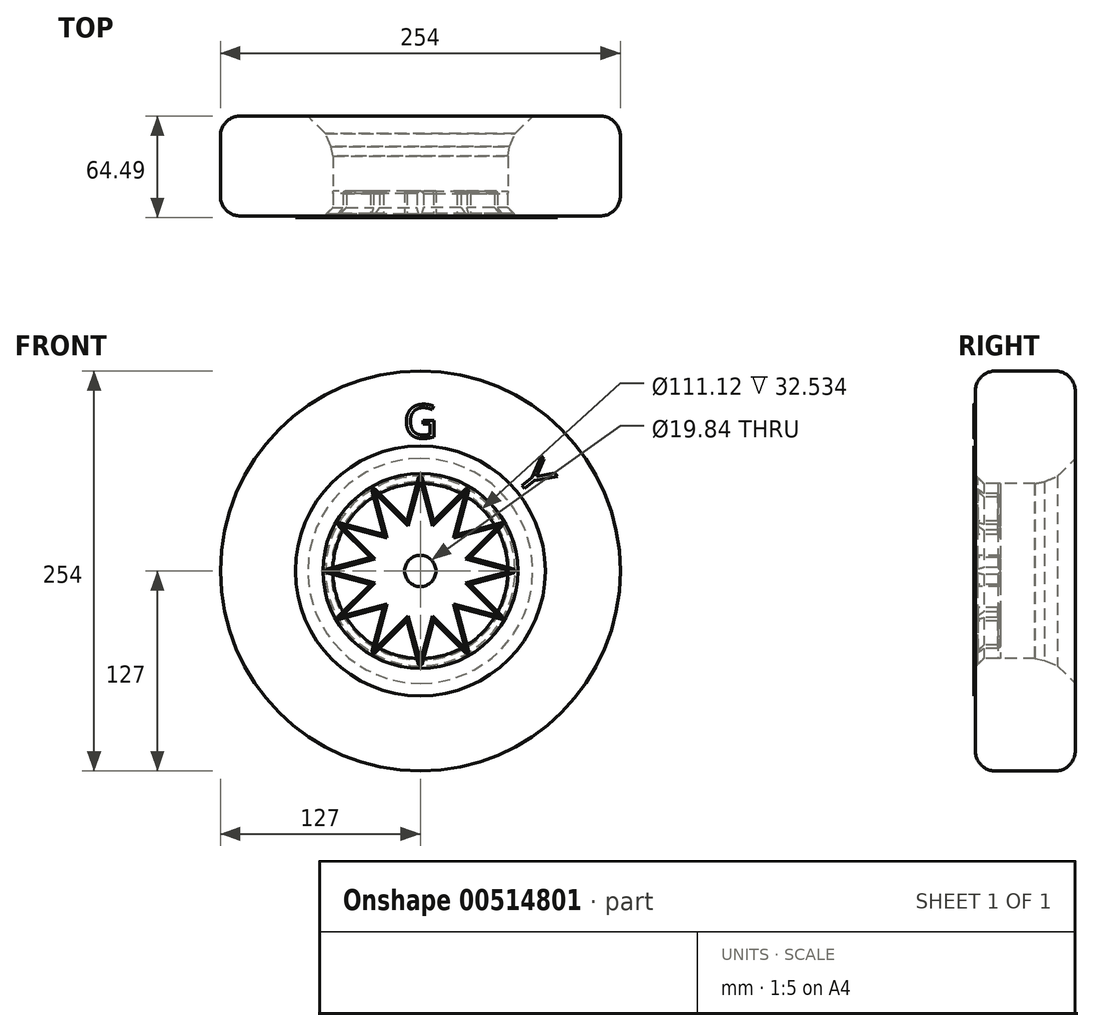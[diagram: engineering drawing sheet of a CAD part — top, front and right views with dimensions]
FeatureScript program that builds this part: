
annotation { "Feature Type Name" : "Feature", "Feature Type Description" : "" }
export const myFeature = defineFeature(function(context is Context, id is Id, definition is map)
    precondition{}
    {
        {
            var Q0;
            Q0=qCreatedBy(makeId("Front.planeOp"),FACE);
            var sketch = newSketch(context, id + "F0", { "sketchPlane" : qUnion([Q0])});
            skCircle(sketch, "E0", {"center": v(0, 0) * mm, "radius": 50.8 * mm});
            skCircle(sketch, "E1", {"center": v(0, 0) * mm, "radius": 31.75 * mm});
            skLineSegment(sketch, "E2", {"start": v(-3.4, 12.7) * mm, "end": v(0, 25.4) * mm});
            skLineSegment(sketch, "E3", {"start": v(3.4, 12.7) * mm, "end": v(0, 25.4) * mm});
            skLineSegment(sketch, "E4", {"start": v(12.7, 22) * mm, "end": v(3.4, 12.7) * mm});
            skLineSegment(sketch, "E5", {"start": v(-25.4, 0) * mm, "end": v(-12.7, 3.4) * mm});
            skLineSegment(sketch, "E6", {"start": v(-22, 12.7) * mm, "end": v(-12.7, 3.4) * mm});
            skLineSegment(sketch, "E7", {"start": v(-25.4, 0) * mm, "end": v(-12.7, -3.4) * mm});
            skLineSegment(sketch, "E8", {"start": v(-22, 12.7) * mm, "end": v(-9.3, 9.3) * mm});
            skLineSegment(sketch, "E9", {"start": v(-12.7, 22) * mm, "end": v(-3.4, 12.7) * mm});
            skLineSegment(sketch, "E10", {"start": v(-12.7, 22) * mm, "end": v(-9.3, 9.3) * mm});
            skLineSegment(sketch, "E11", {"start": v(9.3, 9.3) * mm, "end": v(12.7, 22) * mm});
            skLineSegment(sketch, "E12", {"start": v(9.3, 9.3) * mm, "end": v(22, 12.7) * mm});
            skLineSegment(sketch, "E13", {"start": v(12.7, 3.4) * mm, "end": v(22, 12.7) * mm});
            skLineSegment(sketch, "E14", {"start": v(12.7, 3.4) * mm, "end": v(25.4, 0) * mm});
            skLineSegment(sketch, "E15", {"start": v(12.7, -3.4) * mm, "end": v(25.4, 0) * mm});
            skLineSegment(sketch, "E16", {"start": v(-22, -12.7) * mm, "end": v(-12.7, -3.4) * mm});
            skLineSegment(sketch, "E17", {"start": v(-22, -12.7) * mm, "end": v(-9.3, -9.3) * mm});
            skLineSegment(sketch, "E18", {"start": v(-9.3, -9.3) * mm, "end": v(-12.7, -22) * mm});
            skLineSegment(sketch, "E19", {"start": v(-3.4, -12.7) * mm, "end": v(-12.7, -22) * mm});
            skLineSegment(sketch, "E20", {"start": v(-3.4, -12.7) * mm, "end": v(0, -25.4) * mm});
            skLineSegment(sketch, "E21", {"start": v(3.4, -12.7) * mm, "end": v(0, -25.4) * mm});
            skLineSegment(sketch, "E22", {"start": v(3.4, -12.7) * mm, "end": v(12.7, -22) * mm});
            skLineSegment(sketch, "E23", {"start": v(9.3, -9.3) * mm, "end": v(12.7, -22) * mm});
            skLineSegment(sketch, "E24", {"start": v(9.3, -9.3) * mm, "end": v(22, -12.7) * mm});
            skLineSegment(sketch, "E25", {"start": v(12.7, -3.4) * mm, "end": v(22, -12.7) * mm});
            skCircle(sketch, "E26", {"center": v(0, 0) * mm, "radius": 13.15 * mm});
            skCircle(sketch, "E27", {"center": v(0, 0) * mm, "radius": 9.53 * mm});
            skCircle(sketch, "E28", {"center": v(0, 0) * mm, "radius": 22.23 * mm});
            skCircle(sketch, "E29", {"center": v(0, 0) * mm, "radius": 3.97 * mm});
            skSolve(sketch);
        }
        {
            var Q0;
            {var subQ1=sQuery(id+"F0.wireOp",EDGE,"E2");var subQ3=sQuery(id+"F0.wireOp",EDGE,"E28");var subQ4=makeQuery(id+"F0.imprint","INTERSECT",VERTEX,{"derivedFrom":[subQ1,subQ3]});Q0=makeQuery(id+"F0.imprint","IMPRINT",FACE,{"disambiguationData":[TD([[makeQuery(id+"F0.imprint","IMPRINT",EDGE,{"disambiguationData":[TD([[subQ4,1.0]])],"derivedFrom":subQ3}),1.0]])]});}
            var Q1;
            {var subQ1=sQuery(id+"F0.wireOp",EDGE,"E9");var subQ3=sQuery(id+"F0.wireOp",EDGE,"E28");var subQ4=makeQuery(id+"F0.imprint","INTERSECT",VERTEX,{"derivedFrom":[subQ1,subQ3]});Q1=makeQuery(id+"F0.imprint","IMPRINT",FACE,{"disambiguationData":[TD([[makeQuery(id+"F0.imprint","IMPRINT",EDGE,{"disambiguationData":[TD([[subQ4,-1.0]])],"derivedFrom":subQ3}),1.0]])]});}
            var Q2;
            {var subQ1=sQuery(id+"F0.wireOp",EDGE,"E6");var subQ3=sQuery(id+"F0.wireOp",EDGE,"E28");var subQ4=makeQuery(id+"F0.imprint","INTERSECT",VERTEX,{"derivedFrom":[subQ1,subQ3]});Q2=makeQuery(id+"F0.imprint","IMPRINT",FACE,{"disambiguationData":[TD([[makeQuery(id+"F0.imprint","IMPRINT",EDGE,{"disambiguationData":[TD([[subQ4,1.0]])],"derivedFrom":subQ3}),1.0]])]});}
            var Q3;
            {var subQ1=sQuery(id+"F0.wireOp",EDGE,"E16");var subQ3=sQuery(id+"F0.wireOp",EDGE,"E28");var subQ4=makeQuery(id+"F0.imprint","INTERSECT",VERTEX,{"derivedFrom":[subQ1,subQ3]});Q3=makeQuery(id+"F0.imprint","IMPRINT",FACE,{"disambiguationData":[TD([[makeQuery(id+"F0.imprint","IMPRINT",EDGE,{"disambiguationData":[TD([[subQ4,-1.0]])],"derivedFrom":subQ3}),1.0]])]});}
            var Q4;
            {var subQ1=sQuery(id+"F0.wireOp",EDGE,"E5");var subQ3=sQuery(id+"F0.wireOp",EDGE,"E28");var subQ4=makeQuery(id+"F0.imprint","INTERSECT",VERTEX,{"derivedFrom":[subQ1,subQ3]});Q4=makeQuery(id+"F0.imprint","IMPRINT",FACE,{"disambiguationData":[TD([[makeQuery(id+"F0.imprint","IMPRINT",EDGE,{"disambiguationData":[TD([[subQ4,-1.0]])],"derivedFrom":subQ3}),1.0]])]});}
            var Q5;
            {var subQ1=sQuery(id+"F0.wireOp",EDGE,"E18");var subQ3=sQuery(id+"F0.wireOp",EDGE,"E28");var subQ4=makeQuery(id+"F0.imprint","INTERSECT",VERTEX,{"derivedFrom":[subQ1,subQ3]});Q5=makeQuery(id+"F0.imprint","IMPRINT",FACE,{"disambiguationData":[TD([[makeQuery(id+"F0.imprint","IMPRINT",EDGE,{"disambiguationData":[TD([[subQ4,-1.0]])],"derivedFrom":subQ3}),1.0]])]});}
            var Q6;
            {var subQ1=sQuery(id+"F0.wireOp",EDGE,"E20");var subQ3=sQuery(id+"F0.wireOp",EDGE,"E28");var subQ4=makeQuery(id+"F0.imprint","INTERSECT",VERTEX,{"derivedFrom":[subQ1,subQ3]});Q6=makeQuery(id+"F0.imprint","IMPRINT",FACE,{"disambiguationData":[TD([[makeQuery(id+"F0.imprint","IMPRINT",EDGE,{"disambiguationData":[TD([[subQ4,-1.0]])],"derivedFrom":subQ3}),1.0]])]});}
            var Q7;
            {var subQ1=sQuery(id+"F0.wireOp",EDGE,"E22");var subQ3=sQuery(id+"F0.wireOp",EDGE,"E28");var subQ4=makeQuery(id+"F0.imprint","INTERSECT",VERTEX,{"derivedFrom":[subQ1,subQ3]});Q7=makeQuery(id+"F0.imprint","IMPRINT",FACE,{"disambiguationData":[TD([[makeQuery(id+"F0.imprint","IMPRINT",EDGE,{"disambiguationData":[TD([[subQ4,-1.0]])],"derivedFrom":subQ3}),1.0]])]});}
            var Q8;
            {var subQ1=sQuery(id+"F0.wireOp",EDGE,"E24");var subQ3=sQuery(id+"F0.wireOp",EDGE,"E28");var subQ4=makeQuery(id+"F0.imprint","INTERSECT",VERTEX,{"derivedFrom":[subQ1,subQ3]});Q8=makeQuery(id+"F0.imprint","IMPRINT",FACE,{"disambiguationData":[TD([[makeQuery(id+"F0.imprint","IMPRINT",EDGE,{"disambiguationData":[TD([[subQ4,-1.0]])],"derivedFrom":subQ3}),1.0]])]});}
            var Q9;
            {var subQ1=sQuery(id+"F0.wireOp",EDGE,"E14");var subQ3=sQuery(id+"F0.wireOp",EDGE,"E28");var subQ4=makeQuery(id+"F0.imprint","INTERSECT",VERTEX,{"derivedFrom":[subQ1,subQ3]});Q9=makeQuery(id+"F0.imprint","IMPRINT",FACE,{"disambiguationData":[TD([[makeQuery(id+"F0.imprint","IMPRINT",EDGE,{"disambiguationData":[TD([[subQ4,1.0]])],"derivedFrom":subQ3}),1.0]])]});}
            var Q10;
            {var subQ1=sQuery(id+"F0.wireOp",EDGE,"E12");var subQ3=sQuery(id+"F0.wireOp",EDGE,"E28");var subQ4=makeQuery(id+"F0.imprint","INTERSECT",VERTEX,{"derivedFrom":[subQ1,subQ3]});Q10=makeQuery(id+"F0.imprint","IMPRINT",FACE,{"disambiguationData":[TD([[makeQuery(id+"F0.imprint","IMPRINT",EDGE,{"disambiguationData":[TD([[subQ4,1.0]])],"derivedFrom":subQ3}),1.0]])]});}
            var Q11;
            {var subQ1=sQuery(id+"F0.wireOp",EDGE,"E4");var subQ3=sQuery(id+"F0.wireOp",EDGE,"E28");var subQ4=makeQuery(id+"F0.imprint","INTERSECT",VERTEX,{"derivedFrom":[subQ1,subQ3]});Q11=makeQuery(id+"F0.imprint","IMPRINT",FACE,{"disambiguationData":[TD([[makeQuery(id+"F0.imprint","IMPRINT",EDGE,{"disambiguationData":[TD([[subQ4,1.0]])],"derivedFrom":subQ3}),1.0]])]});}
            var Q12;
            Q12=makeQuery(id+"F0.imprint","IMPRINT",FACE,{"disambiguationData":[TD([[makeQuery(id+"F0.imprint","IMPRINT",EDGE,{"derivedFrom":sQuery(id+"F0.wireOp",EDGE,"E27")}),-1.0]])]});
            extrude(context, id + "F1", {"entities" : qUnion([Q0, Q1, Q2, Q3, Q4, Q5, Q6, Q7, Q8, Q9, Q10, Q11, Q12]), "oppositeDirection" : true, "depth" : 6.35 * mm, "offsetDistance" : 25.4 * mm});
        }
        {
            var Q0;
            Q0=makeQuery(id+"F0.imprint","IMPRINT",FACE,{"disambiguationData":[TD([[makeQuery(id+"F0.imprint","IMPRINT",EDGE,{"derivedFrom":sQuery(id+"F0.wireOp",EDGE,"E1")}),1.0]])]});
            var Q1;
            {var subQ0=sQuery(id+"F0.wireOp",EDGE,"E3");var subQ1=sQuery(id+"F0.wireOp",EDGE,"E2");var subQ2=makeQuery(id+"F0.imprint","INTERSECT",VERTEX,{"derivedFrom":[subQ1,subQ0]});Q1=makeQuery(id+"F0.imprint","IMPRINT",FACE,{"disambiguationData":[TD([[makeQuery(id+"F0.imprint","IMPRINT",EDGE,{"disambiguationData":[TD([[subQ2,1.0]])],"derivedFrom":subQ1}),-1.0]])]});}
            var Q2;
            {var subQ0=sQuery(id+"F0.wireOp",EDGE,"E11");var subQ1=sQuery(id+"F0.wireOp",EDGE,"E4");var subQ2=makeQuery(id+"F0.imprint","INTERSECT",VERTEX,{"derivedFrom":[subQ1,subQ0]});Q2=makeQuery(id+"F0.imprint","IMPRINT",FACE,{"disambiguationData":[TD([[makeQuery(id+"F0.imprint","IMPRINT",EDGE,{"disambiguationData":[TD([[subQ2,-1.0]])],"derivedFrom":subQ1}),1.0]])]});}
            var Q3;
            {var subQ0=sQuery(id+"F0.wireOp",EDGE,"E10");var subQ1=sQuery(id+"F0.wireOp",EDGE,"E9");var subQ2=makeQuery(id+"F0.imprint","INTERSECT",VERTEX,{"derivedFrom":[subQ1,subQ0]});Q3=makeQuery(id+"F0.imprint","IMPRINT",FACE,{"disambiguationData":[TD([[makeQuery(id+"F0.imprint","IMPRINT",EDGE,{"disambiguationData":[TD([[subQ2,-1.0]])],"derivedFrom":subQ1}),-1.0]])]});}
            var Q4;
            {var subQ0=sQuery(id+"F0.wireOp",EDGE,"E8");var subQ1=sQuery(id+"F0.wireOp",EDGE,"E6");var subQ2=makeQuery(id+"F0.imprint","INTERSECT",VERTEX,{"derivedFrom":[subQ1,subQ0]});Q4=makeQuery(id+"F0.imprint","IMPRINT",FACE,{"disambiguationData":[TD([[makeQuery(id+"F0.imprint","IMPRINT",EDGE,{"disambiguationData":[TD([[subQ2,-1.0]])],"derivedFrom":subQ1}),1.0]])]});}
            var Q5;
            {var subQ0=sQuery(id+"F0.wireOp",EDGE,"E7");var subQ1=sQuery(id+"F0.wireOp",EDGE,"E5");var subQ2=makeQuery(id+"F0.imprint","INTERSECT",VERTEX,{"derivedFrom":[subQ1,subQ0]});Q5=makeQuery(id+"F0.imprint","IMPRINT",FACE,{"disambiguationData":[TD([[makeQuery(id+"F0.imprint","IMPRINT",EDGE,{"disambiguationData":[TD([[subQ2,-1.0]])],"derivedFrom":subQ1}),-1.0]])]});}
            var Q6;
            {var subQ0=sQuery(id+"F0.wireOp",EDGE,"E13");var subQ1=sQuery(id+"F0.wireOp",EDGE,"E12");var subQ2=makeQuery(id+"F0.imprint","INTERSECT",VERTEX,{"derivedFrom":[subQ1,subQ0]});Q6=makeQuery(id+"F0.imprint","IMPRINT",FACE,{"disambiguationData":[TD([[makeQuery(id+"F0.imprint","IMPRINT",EDGE,{"disambiguationData":[TD([[subQ2,1.0]])],"derivedFrom":subQ1}),-1.0]])]});}
            var Q7;
            {var subQ0=sQuery(id+"F0.wireOp",EDGE,"E15");var subQ1=sQuery(id+"F0.wireOp",EDGE,"E14");var subQ2=makeQuery(id+"F0.imprint","INTERSECT",VERTEX,{"derivedFrom":[subQ1,subQ0]});Q7=makeQuery(id+"F0.imprint","IMPRINT",FACE,{"disambiguationData":[TD([[makeQuery(id+"F0.imprint","IMPRINT",EDGE,{"disambiguationData":[TD([[subQ2,1.0]])],"derivedFrom":subQ1}),-1.0]])]});}
            var Q8;
            {var subQ0=sQuery(id+"F0.wireOp",EDGE,"E25");var subQ1=sQuery(id+"F0.wireOp",EDGE,"E24");var subQ2=makeQuery(id+"F0.imprint","INTERSECT",VERTEX,{"derivedFrom":[subQ1,subQ0]});Q8=makeQuery(id+"F0.imprint","IMPRINT",FACE,{"disambiguationData":[TD([[makeQuery(id+"F0.imprint","IMPRINT",EDGE,{"disambiguationData":[TD([[subQ2,1.0]])],"derivedFrom":subQ1}),1.0]])]});}
            var Q9;
            {var subQ0=sQuery(id+"F0.wireOp",EDGE,"E23");var subQ1=sQuery(id+"F0.wireOp",EDGE,"E22");var subQ2=makeQuery(id+"F0.imprint","INTERSECT",VERTEX,{"derivedFrom":[subQ1,subQ0]});Q9=makeQuery(id+"F0.imprint","IMPRINT",FACE,{"disambiguationData":[TD([[makeQuery(id+"F0.imprint","IMPRINT",EDGE,{"disambiguationData":[TD([[subQ2,1.0]])],"derivedFrom":subQ1}),1.0]])]});}
            var Q10;
            {var subQ0=sQuery(id+"F0.wireOp",EDGE,"E19");var subQ1=sQuery(id+"F0.wireOp",EDGE,"E18");var subQ2=makeQuery(id+"F0.imprint","INTERSECT",VERTEX,{"derivedFrom":[subQ1,subQ0]});Q10=makeQuery(id+"F0.imprint","IMPRINT",FACE,{"disambiguationData":[TD([[makeQuery(id+"F0.imprint","IMPRINT",EDGE,{"disambiguationData":[TD([[subQ2,1.0]])],"derivedFrom":subQ1}),1.0]])]});}
            var Q11;
            {var subQ0=sQuery(id+"F0.wireOp",EDGE,"E17");var subQ1=sQuery(id+"F0.wireOp",EDGE,"E16");var subQ2=makeQuery(id+"F0.imprint","INTERSECT",VERTEX,{"derivedFrom":[subQ1,subQ0]});Q11=makeQuery(id+"F0.imprint","IMPRINT",FACE,{"disambiguationData":[TD([[makeQuery(id+"F0.imprint","IMPRINT",EDGE,{"disambiguationData":[TD([[subQ2,-1.0]])],"derivedFrom":subQ1}),-1.0]])]});}
            var Q12;
            {var subQ0=sQuery(id+"F0.wireOp",EDGE,"E21");var subQ1=sQuery(id+"F0.wireOp",EDGE,"E20");var subQ2=makeQuery(id+"F0.imprint","INTERSECT",VERTEX,{"derivedFrom":[subQ1,subQ0]});Q12=makeQuery(id+"F0.imprint","IMPRINT",FACE,{"disambiguationData":[TD([[makeQuery(id+"F0.imprint","IMPRINT",EDGE,{"disambiguationData":[TD([[subQ2,1.0]])],"derivedFrom":subQ1}),1.0]])]});}
            extrude(context, id + "F2", {"entities" : qUnion([Q0, Q1, Q2, Q3, Q4, Q5, Q6, Q7, Q8, Q9, Q10, Q11, Q12]), "operationType" : NewBodyOperationType.ADD, "oppositeDirection" : true, "depth" : 25.4 * mm, "offsetDistance" : 25.4 * mm});
        }
        {
            var Q0;
            Q0=makeQuery(id+"F0.imprint","IMPRINT",FACE,{"disambiguationData":[TD([[makeQuery(id+"F0.imprint","IMPRINT",EDGE,{"derivedFrom":sQuery(id+"F0.wireOp",EDGE,"E0")}),1.0]])]});
            extrude(context, id + "F3", {"entities" : qUnion([Q0]), "oppositeDirection" : true, "depth" : 25.4 * mm, "offsetDistance" : 25.4 * mm});
        }
        {
            var Q0;
            Q0=makeQuery(id+"F3.opExtrude","CAP_EDGE",EDGE,{"disambiguationData":[OSD([sQuery(id+"F0.wireOp",EDGE,"E0")])],"isStart":true});
            var Q1;
            Q1=makeQuery(id+"F3.opExtrude","CAP_EDGE",EDGE,{"disambiguationData":[OSD([sQuery(id+"F0.wireOp",EDGE,"E0")])],"isStart":false});
            fillet(context, id + "F4", {"entities" : qUnion([Q0, Q1]), "radius" : 5.08 * mm, "tangentPropagation" : true, "allowEdgeOverflow" : false});
        }
        {
            var Q0;
            Q0=makeQuery(id+"F1.opExtrude","CAP_EDGE",EDGE,{"disambiguationData":[OSD([sQuery(id+"F0.wireOp",EDGE,"E4")])],"isStart":true});
            var Q1;
            Q1=makeQuery(id+"F1.opExtrude","CAP_EDGE",EDGE,{"disambiguationData":[OSD([sQuery(id+"F0.wireOp",EDGE,"E3")])],"isStart":true});
            var Q2;
            Q2=makeQuery(id+"F1.opExtrude","CAP_EDGE",EDGE,{"disambiguationData":[OSD([sQuery(id+"F0.wireOp",EDGE,"E2")])],"isStart":true});
            var Q3;
            Q3=makeQuery(id+"F1.opExtrude","CAP_EDGE",EDGE,{"disambiguationData":[OSD([sQuery(id+"F0.wireOp",EDGE,"E9")])],"isStart":true});
            var Q4;
            Q4=makeQuery(id+"F1.opExtrude","CAP_EDGE",EDGE,{"disambiguationData":[OSD([sQuery(id+"F0.wireOp",EDGE,"E10")])],"isStart":true});
            var Q5;
            Q5=makeQuery(id+"F1.opExtrude","CAP_EDGE",EDGE,{"disambiguationData":[OSD([sQuery(id+"F0.wireOp",EDGE,"E11")])],"isStart":true});
            var Q6;
            Q6=makeQuery(id+"F1.opExtrude","CAP_EDGE",EDGE,{"disambiguationData":[OSD([sQuery(id+"F0.wireOp",EDGE,"E12")])],"isStart":true});
            var Q7;
            Q7=makeQuery(id+"F1.opExtrude","CAP_EDGE",EDGE,{"disambiguationData":[OSD([sQuery(id+"F0.wireOp",EDGE,"E13")])],"isStart":true});
            var Q8;
            Q8=makeQuery(id+"F1.opExtrude","CAP_EDGE",EDGE,{"disambiguationData":[OSD([sQuery(id+"F0.wireOp",EDGE,"E14")])],"isStart":true});
            var Q9;
            Q9=makeQuery(id+"F1.opExtrude","CAP_EDGE",EDGE,{"disambiguationData":[OSD([sQuery(id+"F0.wireOp",EDGE,"E15")])],"isStart":true});
            var Q10;
            Q10=makeQuery(id+"F1.opExtrude","CAP_EDGE",EDGE,{"disambiguationData":[OSD([sQuery(id+"F0.wireOp",EDGE,"E8")])],"isStart":true});
            var Q11;
            Q11=makeQuery(id+"F1.opExtrude","CAP_EDGE",EDGE,{"disambiguationData":[OSD([sQuery(id+"F0.wireOp",EDGE,"E6")])],"isStart":true});
            var Q12;
            Q12=makeQuery(id+"F1.opExtrude","CAP_EDGE",EDGE,{"disambiguationData":[OSD([sQuery(id+"F0.wireOp",EDGE,"E5")])],"isStart":true});
            var Q13;
            Q13=makeQuery(id+"F1.opExtrude","CAP_EDGE",EDGE,{"disambiguationData":[OSD([sQuery(id+"F0.wireOp",EDGE,"E7")])],"isStart":true});
            var Q14;
            Q14=makeQuery(id+"F1.opExtrude","CAP_EDGE",EDGE,{"disambiguationData":[OSD([sQuery(id+"F0.wireOp",EDGE,"E16")])],"isStart":true});
            var Q15;
            Q15=makeQuery(id+"F1.opExtrude","CAP_EDGE",EDGE,{"disambiguationData":[OSD([sQuery(id+"F0.wireOp",EDGE,"E17")])],"isStart":true});
            var Q16;
            Q16=makeQuery(id+"F1.opExtrude","CAP_EDGE",EDGE,{"disambiguationData":[OSD([sQuery(id+"F0.wireOp",EDGE,"E18")])],"isStart":true});
            var Q17;
            Q17=makeQuery(id+"F1.opExtrude","CAP_EDGE",EDGE,{"disambiguationData":[OSD([sQuery(id+"F0.wireOp",EDGE,"E25")])],"isStart":true});
            var Q18;
            Q18=makeQuery(id+"F1.opExtrude","CAP_EDGE",EDGE,{"disambiguationData":[OSD([sQuery(id+"F0.wireOp",EDGE,"E19")])],"isStart":true});
            var Q19;
            Q19=makeQuery(id+"F1.opExtrude","CAP_EDGE",EDGE,{"disambiguationData":[OSD([sQuery(id+"F0.wireOp",EDGE,"E20")])],"isStart":true});
            var Q20;
            Q20=makeQuery(id+"F1.opExtrude","CAP_EDGE",EDGE,{"disambiguationData":[OSD([sQuery(id+"F0.wireOp",EDGE,"E21")])],"isStart":true});
            var Q21;
            Q21=makeQuery(id+"F1.opExtrude","CAP_EDGE",EDGE,{"disambiguationData":[OSD([sQuery(id+"F0.wireOp",EDGE,"E22")])],"isStart":true});
            var Q22;
            Q22=makeQuery(id+"F1.opExtrude","CAP_EDGE",EDGE,{"disambiguationData":[OSD([sQuery(id+"F0.wireOp",EDGE,"E23")])],"isStart":true});
            var Q23;
            Q23=makeQuery(id+"F1.opExtrude","CAP_EDGE",EDGE,{"disambiguationData":[OSD([sQuery(id+"F0.wireOp",EDGE,"E24")])],"isStart":true});
            var Q24;
            Q24=makeQuery(id+"F1.opExtrude","CAP_EDGE",EDGE,{"disambiguationData":[OSD([sQuery(id+"F0.wireOp",EDGE,"E12")])],"isStart":false});
            var Q25;
            Q25=makeQuery(id+"F1.opExtrude","CAP_EDGE",EDGE,{"disambiguationData":[OSD([sQuery(id+"F0.wireOp",EDGE,"E13")])],"isStart":false});
            var Q26;
            Q26=makeQuery(id+"F1.opExtrude","CAP_EDGE",EDGE,{"disambiguationData":[OSD([sQuery(id+"F0.wireOp",EDGE,"E14")])],"isStart":false});
            var Q27;
            Q27=makeQuery(id+"F1.opExtrude","CAP_EDGE",EDGE,{"disambiguationData":[OSD([sQuery(id+"F0.wireOp",EDGE,"E15")])],"isStart":false});
            var Q28;
            Q28=makeQuery(id+"F1.opExtrude","CAP_EDGE",EDGE,{"disambiguationData":[OSD([sQuery(id+"F0.wireOp",EDGE,"E25")])],"isStart":false});
            var Q29;
            Q29=makeQuery(id+"F1.opExtrude","CAP_EDGE",EDGE,{"disambiguationData":[OSD([sQuery(id+"F0.wireOp",EDGE,"E24")])],"isStart":false});
            var Q30;
            Q30=makeQuery(id+"F1.opExtrude","CAP_EDGE",EDGE,{"disambiguationData":[OSD([sQuery(id+"F0.wireOp",EDGE,"E23")])],"isStart":false});
            var Q31;
            Q31=makeQuery(id+"F1.opExtrude","CAP_EDGE",EDGE,{"disambiguationData":[OSD([sQuery(id+"F0.wireOp",EDGE,"E22")])],"isStart":false});
            var Q32;
            Q32=makeQuery(id+"F1.opExtrude","CAP_EDGE",EDGE,{"disambiguationData":[OSD([sQuery(id+"F0.wireOp",EDGE,"E21")])],"isStart":false});
            var Q33;
            Q33=makeQuery(id+"F1.opExtrude","CAP_EDGE",EDGE,{"disambiguationData":[OSD([sQuery(id+"F0.wireOp",EDGE,"E20")])],"isStart":false});
            var Q34;
            Q34=makeQuery(id+"F1.opExtrude","CAP_EDGE",EDGE,{"disambiguationData":[OSD([sQuery(id+"F0.wireOp",EDGE,"E19")])],"isStart":false});
            var Q35;
            Q35=makeQuery(id+"F1.opExtrude","CAP_EDGE",EDGE,{"disambiguationData":[OSD([sQuery(id+"F0.wireOp",EDGE,"E11")])],"isStart":false});
            var Q36;
            Q36=makeQuery(id+"F1.opExtrude","CAP_EDGE",EDGE,{"disambiguationData":[OSD([sQuery(id+"F0.wireOp",EDGE,"E9")])],"isStart":false});
            var Q37;
            Q37=makeQuery(id+"F1.opExtrude","CAP_EDGE",EDGE,{"disambiguationData":[OSD([sQuery(id+"F0.wireOp",EDGE,"E2")])],"isStart":false});
            var Q38;
            Q38=makeQuery(id+"F1.opExtrude","CAP_EDGE",EDGE,{"disambiguationData":[OSD([sQuery(id+"F0.wireOp",EDGE,"E3")])],"isStart":false});
            var Q39;
            Q39=makeQuery(id+"F1.opExtrude","CAP_EDGE",EDGE,{"disambiguationData":[OSD([sQuery(id+"F0.wireOp",EDGE,"E4")])],"isStart":false});
            var Q40;
            Q40=makeQuery(id+"F1.opExtrude","CAP_EDGE",EDGE,{"disambiguationData":[OSD([sQuery(id+"F0.wireOp",EDGE,"E18")])],"isStart":false});
            var Q41;
            Q41=makeQuery(id+"F1.opExtrude","CAP_EDGE",EDGE,{"disambiguationData":[OSD([sQuery(id+"F0.wireOp",EDGE,"E17")])],"isStart":false});
            var Q42;
            Q42=makeQuery(id+"F1.opExtrude","CAP_EDGE",EDGE,{"disambiguationData":[OSD([sQuery(id+"F0.wireOp",EDGE,"E16")])],"isStart":false});
            var Q43;
            Q43=makeQuery(id+"F1.opExtrude","CAP_EDGE",EDGE,{"disambiguationData":[OSD([sQuery(id+"F0.wireOp",EDGE,"E10")])],"isStart":false});
            var Q44;
            Q44=makeQuery(id+"F1.opExtrude","CAP_EDGE",EDGE,{"disambiguationData":[OSD([sQuery(id+"F0.wireOp",EDGE,"E8")])],"isStart":false});
            var Q45;
            Q45=makeQuery(id+"F1.opExtrude","CAP_EDGE",EDGE,{"disambiguationData":[OSD([sQuery(id+"F0.wireOp",EDGE,"E6")])],"isStart":false});
            var Q46;
            Q46=makeQuery(id+"F1.opExtrude","CAP_EDGE",EDGE,{"disambiguationData":[OSD([sQuery(id+"F0.wireOp",EDGE,"E5")])],"isStart":false});
            var Q47;
            Q47=makeQuery(id+"F1.opExtrude","CAP_EDGE",EDGE,{"disambiguationData":[OSD([sQuery(id+"F0.wireOp",EDGE,"E7")])],"isStart":false});
            chamfer(context, id + "F5", {"entities" : qUnion([Q0, Q1, Q2, Q3, Q4, Q5, Q6, Q7, Q8, Q9, Q10, Q11, Q12, Q13, Q14, Q15, Q16, Q17, Q18, Q19, Q20, Q21, Q22, Q23, Q24, Q25, Q26, Q27, Q28, Q29, Q30, Q31, Q32, Q33, Q34, Q35, Q36, Q37, Q38, Q39, Q40, Q41, Q42, Q43, Q44, Q45, Q46, Q47]), "width" : 0.64 * mm, "tangentPropagation" : true});
        }
        {
            var Q0;
            {var subQ0=sQuery(id+"F0.wireOp",EDGE,"E28");Q0=makeQuery(id+"F2.boolean.opBoolean","MERGE",FACE,{"derivedFrom":[makeQuery(id+"F1.opExtrude","CAP_FACE",FACE,{"disambiguationData":[OSD([sQuery(id+"F0.wireOp",EDGE,"E2"),sQuery(id+"F0.wireOp",EDGE,"E3"),sQuery(id+"F0.wireOp",EDGE,"E4"),sQuery(id+"F0.wireOp",EDGE,"E5"),sQuery(id+"F0.wireOp",EDGE,"E6"),sQuery(id+"F0.wireOp",EDGE,"E7"),sQuery(id+"F0.wireOp",EDGE,"E8"),sQuery(id+"F0.wireOp",EDGE,"E9"),sQuery(id+"F0.wireOp",EDGE,"E10"),sQuery(id+"F0.wireOp",EDGE,"E11"),sQuery(id+"F0.wireOp",EDGE,"E12"),sQuery(id+"F0.wireOp",EDGE,"E13"),sQuery(id+"F0.wireOp",EDGE,"E14"),sQuery(id+"F0.wireOp",EDGE,"E15"),sQuery(id+"F0.wireOp",EDGE,"E16"),sQuery(id+"F0.wireOp",EDGE,"E17"),sQuery(id+"F0.wireOp",EDGE,"E18"),sQuery(id+"F0.wireOp",EDGE,"E19"),sQuery(id+"F0.wireOp",EDGE,"E20"),sQuery(id+"F0.wireOp",EDGE,"E21"),sQuery(id+"F0.wireOp",EDGE,"E22"),sQuery(id+"F0.wireOp",EDGE,"E23"),sQuery(id+"F0.wireOp",EDGE,"E24"),sQuery(id+"F0.wireOp",EDGE,"E25"),sQuery(id+"F0.wireOp",EDGE,"E27"),subQ0])],"isStart":true}),makeQuery(id+"F2.opExtrude","CAP_FACE",FACE,{"disambiguationData":[OSD([sQuery(id+"F0.wireOp",EDGE,"E1"),subQ0])],"isStart":true})]});}
            var sketch = newSketch(context, id + "F6", { "sketchPlane" : qUnion([Q0])});
            skCircle(sketch, "E30", {"center": v(165.08, 26.99) * mm, "radius": 1.59 * mm});
            skSolve(sketch);
        }
        {
            var Q0;
            Q0=makeQuery(id+"F6.imprint","IMPRINT",FACE,{"disambiguationData":[TD([[makeQuery(id+"F6.imprint","IMPRINT",EDGE,{"derivedFrom":sQuery(id+"F6.wireOp",EDGE,"E30")}),1.0]])]});
            extrude(context, id + "F7", {"entities" : qUnion([Q0]), "operationType" : NewBodyOperationType.ADD, "depth" : 0.8 * mm, "offsetDistance" : 25.4 * mm});
        }
        {
            var Q0;
            Q0=makeQuery(id+"F0.imprint","IMPRINT",FACE,{"disambiguationData":[TD([[makeQuery(id+"F0.imprint","IMPRINT",EDGE,{"derivedFrom":sQuery(id+"F0.wireOp",EDGE,"E27")}),1.0]])]});
            extrude(context, id + "F8", {"entities" : qUnion([Q0]), "operationType" : NewBodyOperationType.ADD, "oppositeDirection" : true, "depth" : 6.35 * mm, "offsetDistance" : 25.4 * mm});
        }
        {
            var Q0;
            {var subQ0=sQuery(id+"F0.wireOp",EDGE,"E27");var subQ1=sQuery(id+"F0.wireOp",EDGE,"E28");Q0=makeQuery(id+"F8.boolean.opBoolean","MERGE",FACE,{"derivedFrom":[makeQuery(id+"F2.boolean.opBoolean","MERGE",FACE,{"derivedFrom":[makeQuery(id+"F1.opExtrude","CAP_FACE",FACE,{"disambiguationData":[OSD([sQuery(id+"F0.wireOp",EDGE,"E2"),sQuery(id+"F0.wireOp",EDGE,"E3"),sQuery(id+"F0.wireOp",EDGE,"E4"),sQuery(id+"F0.wireOp",EDGE,"E5"),sQuery(id+"F0.wireOp",EDGE,"E6"),sQuery(id+"F0.wireOp",EDGE,"E7"),sQuery(id+"F0.wireOp",EDGE,"E8"),sQuery(id+"F0.wireOp",EDGE,"E9"),sQuery(id+"F0.wireOp",EDGE,"E10"),sQuery(id+"F0.wireOp",EDGE,"E11"),sQuery(id+"F0.wireOp",EDGE,"E12"),sQuery(id+"F0.wireOp",EDGE,"E13"),sQuery(id+"F0.wireOp",EDGE,"E14"),sQuery(id+"F0.wireOp",EDGE,"E15"),sQuery(id+"F0.wireOp",EDGE,"E16"),sQuery(id+"F0.wireOp",EDGE,"E17"),sQuery(id+"F0.wireOp",EDGE,"E18"),sQuery(id+"F0.wireOp",EDGE,"E19"),sQuery(id+"F0.wireOp",EDGE,"E20"),sQuery(id+"F0.wireOp",EDGE,"E21"),sQuery(id+"F0.wireOp",EDGE,"E22"),sQuery(id+"F0.wireOp",EDGE,"E23"),sQuery(id+"F0.wireOp",EDGE,"E24"),sQuery(id+"F0.wireOp",EDGE,"E25"),subQ0,subQ1])],"isStart":true}),makeQuery(id+"F2.opExtrude","CAP_FACE",FACE,{"disambiguationData":[OSD([sQuery(id+"F0.wireOp",EDGE,"E1"),subQ1])],"isStart":true})]}),makeQuery(id+"F8.opExtrude","CAP_FACE",FACE,{"disambiguationData":[OSD([subQ0,sQuery(id+"F0.wireOp",EDGE,"E29")])],"isStart":true})]});}
            var sketch = newSketch(context, id + "F9", { "sketchPlane" : qUnion([Q0])});
            skPoint(sketch, "E31", {"position": v(164.5, 7.54) * mm});
            skPoint(sketch, "E32", {"position": v(170, 5.74) * mm});
            skPoint(sketch, "E33", {"position": v(172.62, 0.58) * mm});
            skPoint(sketch, "E34", {"position": v(170.83, -4.92) * mm});
            skPoint(sketch, "E35", {"position": v(165.67, -7.54) * mm});
            skPoint(sketch, "E36", {"position": v(160.17, -5.74) * mm});
            skPoint(sketch, "E37", {"position": v(157.54, -0.58) * mm});
            skPoint(sketch, "E38", {"position": v(159.34, 4.92) * mm});
            skCircle(sketch, "E39", {"center": v(0, 0) * mm, "radius": 22.23 * mm});
            skSolve(sketch);
        }
        {
            var Q0;
            Q0=makeQuery(id+"F2.opExtrude","CAP_EDGE",EDGE,{"disambiguationData":[OSD([sQuery(id+"F0.wireOp",EDGE,"E28")])],"isStart":false});
            chamfer(context, id + "F10", {"entities" : qUnion([Q0]), "width" : 6.35 * mm, "tangentPropagation" : true});
        }
        {
            var Q0;
            {var subQ0=sQuery(id+"F0.wireOp",EDGE,"E1");Q0=makeQuery(id+"F9.imprint","IMPRINT",FACE,{"disambiguationData":[TD([[makeQuery(id+"F9.imprint","IMPRINT",EDGE,{"derivedFrom":makeQuery(id+"F2.opExtrude","CAP_EDGE",EDGE,{"disambiguationData":[OSD([subQ0])],"isStart":true})}),1.0]])]});}
            extrude(context, id + "F11", {"entities" : qUnion([Q0]), "operationType" : NewBodyOperationType.ADD, "depth" : 0.4 * mm, "offsetDistance" : 25.4 * mm});
        }
        {
            var Q0;
            Q0=makeQuery(id+"F11.opExtrude","CAP_EDGE",EDGE,{"disambiguationData":[OSD([sQuery(id+"F9.wireOp",EDGE,"E39")])],"isStart":false});
            chamfer(context, id + "F12", {"entities" : qUnion([Q0]), "width" : 2.54 * mm, "tangentPropagation" : true});
        }
        {
            var Q0;
            {var subQ0=sQuery(id+"F0.wireOp",EDGE,"E28");Q0=makeQuery(id+"F10.opChamfer","BLEND_EDGE",EDGE,{"blendedFrom":[makeQuery(id+"F2.opExtrude","CAP_EDGE",EDGE,{"disambiguationData":[OSD([subQ0])],"isStart":false}),makeQuery(id+"F2.opExtrude","SWEPT_FACE",FACE,{"disambiguationData":[OSD([subQ0])]})],"blendedInto":[makeQuery(id+"F2.opExtrude","SWEPT_FACE",FACE,{"disambiguationData":[OSD([subQ0])]})]});}
            chamfer(context, id + "F13", {"entities" : qUnion([Q0]), "width" : 6.35 * mm, "tangentPropagation" : true});
        }
        {
            var Q0;
            {var subQ0=sQuery(id+"F0.wireOp",EDGE,"E28");var subQ1=makeQuery(id+"F2.opExtrude","SWEPT_FACE",FACE,{"disambiguationData":[OSD([subQ0])]});Q0=makeQuery(id+"F13.opChamfer","BLEND_EDGE",EDGE,{"blendedFrom":[makeQuery(id+"F10.opChamfer","BLEND_EDGE",EDGE,{"blendedFrom":[makeQuery(id+"F2.opExtrude","CAP_EDGE",EDGE,{"disambiguationData":[OSD([subQ0])],"isStart":false}),subQ1],"blendedInto":[subQ1]}),makeQuery(id+"F11.boolean.opBoolean","MERGE",FACE,{"derivedFrom":[subQ1,makeQuery(id+"F11.opExtrude","SWEPT_FACE",FACE,{"disambiguationData":[OSD([sQuery(id+"F9.wireOp",EDGE,"E39")])]})]})],"blendedInto":[makeQuery(id+"F11.boolean.opBoolean","MERGE",FACE,{"derivedFrom":[subQ1,makeQuery(id+"F11.opExtrude","SWEPT_FACE",FACE,{"disambiguationData":[OSD([sQuery(id+"F9.wireOp",EDGE,"E39")])]})]})]});}
            chamfer(context, id + "F14", {"entities" : qUnion([Q0]), "width" : 6.35 * mm, "tangentPropagation" : true});
        }
        {
            var Q0;
            Q0=makeQuery(id+"F7.opExtrude","SWEPT_BODY",BODY,{"disambiguationData":[OSD([sQuery(id+"F6.wireOp",EDGE,"E30")])]});
            deleteBodies(context, id + "F15", {"entities" : qUnion([Q0])});
        }
        {
            var Q0;
            Q0=makeQuery(id+"F3.opExtrude","CAP_FACE",FACE,{"disambiguationData":[OSD([sQuery(id+"F0.wireOp",EDGE,"E0"),sQuery(id+"F0.wireOp",EDGE,"E1")])],"isStart":true});
            var sketch = newSketch(context, id + "F16", { "sketchPlane" : qUnion([Q0])});
            skText(sketch, "E40", { "text": "G\n", "fontName": "OpenSans-Regular.ttf"});
            skPoint(sketch, "E41", {"position": v(-4.27, 42.33) * mm});
            skPoint(sketch, "E42", {"position": v(4.27, 42.33) * mm});
            skPoint(sketch, "E43", {"position": v(4.27, 33.78) * mm});
            skPoint(sketch, "E44", {"position": v(-4.27, 33.78) * mm});
            skPoint(sketch, "E45.1.0", {"position": v(-30.43, 29.73) * mm});
            skPoint(sketch, "E45.1.1", {"position": v(-35.76, 23.05) * mm});
            skPoint(sketch, "E45.1.2", {"position": v(-29.08, 17.72) * mm});
            skPoint(sketch, "E45.1.3", {"position": v(-23.75, 24.4) * mm});
            skPoint(sketch, "E45.2.0", {"position": v(-42.22, -5.25) * mm});
            skPoint(sketch, "E45.2.1", {"position": v(-40.32, -13.58) * mm});
            skPoint(sketch, "E45.2.2", {"position": v(-31.98, -11.68) * mm});
            skPoint(sketch, "E45.2.3", {"position": v(-33.89, -3.35) * mm});
            skPoint(sketch, "E45.3.0", {"position": v(-22.21, -36.28) * mm});
            skPoint(sketch, "E45.3.1", {"position": v(-14.52, -40) * mm});
            skPoint(sketch, "E45.3.2", {"position": v(-10.8, -32.29) * mm});
            skPoint(sketch, "E45.3.3", {"position": v(-18.5, -28.58) * mm});
            skPoint(sketch, "E45.4.0", {"position": v(14.52, -40) * mm});
            skPoint(sketch, "E45.4.1", {"position": v(22.21, -36.28) * mm});
            skPoint(sketch, "E45.4.2", {"position": v(18.5, -28.58) * mm});
            skPoint(sketch, "E45.4.3", {"position": v(10.8, -32.29) * mm});
            skPoint(sketch, "E45.5.0", {"position": v(40.32, -13.58) * mm});
            skPoint(sketch, "E45.5.1", {"position": v(42.22, -5.25) * mm});
            skPoint(sketch, "E45.5.2", {"position": v(33.89, -3.35) * mm});
            skPoint(sketch, "E45.5.3", {"position": v(31.98, -11.68) * mm});
            skPoint(sketch, "E45.6.0", {"position": v(35.76, 23.05) * mm});
            skPoint(sketch, "E45.6.1", {"position": v(30.43, 29.73) * mm});
            skPoint(sketch, "E45.6.2", {"position": v(23.75, 24.4) * mm});
            skPoint(sketch, "E45.6.3", {"position": v(29.08, 17.72) * mm});
            skPoint(sketch, "E45.center", {"position": v(0, 0) * mm});
            skText(sketch, "E46", { "text": "Y", "fontName": "OpenSans-Regular.ttf"});
            skPoint(sketch, "E47", {"position": v(29.75, 23.73) * mm});
            const initialGuessF16  = {"E40": [-0.00427, 0.03378, 1, 0, 0.00855], "E46": [0.0241, 0.02396, 0.62349, -0.78183, 0.00855]};
            skSetInitialGuess(sketch, initialGuessF16);
            skSolve(sketch);
        }
        {
            var Q0;
            Q0 = qSketchRegion(id + "F16", true);
            extrude(context, id + "F17", {"entities" : qUnion([Q0]), "operationType" : NewBodyOperationType.ADD, "depth" : 0.4 * mm, "offsetDistance" : 25.4 * mm});
        }
        {
            var Q0;
            Q0=makeQuery(id+"F1.opExtrude","SWEPT_BODY",BODY,{"disambiguationData":[OSD([sQuery(id+"F0.wireOp",EDGE,"E2"),sQuery(id+"F0.wireOp",EDGE,"E3"),sQuery(id+"F0.wireOp",EDGE,"E4"),sQuery(id+"F0.wireOp",EDGE,"E5"),sQuery(id+"F0.wireOp",EDGE,"E6"),sQuery(id+"F0.wireOp",EDGE,"E7"),sQuery(id+"F0.wireOp",EDGE,"E8"),sQuery(id+"F0.wireOp",EDGE,"E9"),sQuery(id+"F0.wireOp",EDGE,"E10"),sQuery(id+"F0.wireOp",EDGE,"E11"),sQuery(id+"F0.wireOp",EDGE,"E12"),sQuery(id+"F0.wireOp",EDGE,"E13"),sQuery(id+"F0.wireOp",EDGE,"E14"),sQuery(id+"F0.wireOp",EDGE,"E15"),sQuery(id+"F0.wireOp",EDGE,"E16"),sQuery(id+"F0.wireOp",EDGE,"E17"),sQuery(id+"F0.wireOp",EDGE,"E18"),sQuery(id+"F0.wireOp",EDGE,"E19"),sQuery(id+"F0.wireOp",EDGE,"E20"),sQuery(id+"F0.wireOp",EDGE,"E21"),sQuery(id+"F0.wireOp",EDGE,"E22"),sQuery(id+"F0.wireOp",EDGE,"E23"),sQuery(id+"F0.wireOp",EDGE,"E24"),sQuery(id+"F0.wireOp",EDGE,"E25"),sQuery(id+"F0.wireOp",EDGE,"E27"),sQuery(id+"F0.wireOp",EDGE,"E28")])]});
            var Q1;
            Q1=makeQuery(id+"F3.opExtrude","SWEPT_BODY",BODY,{"disambiguationData":[OSD([sQuery(id+"F0.wireOp",EDGE,"E0"),sQuery(id+"F0.wireOp",EDGE,"E1")])]});
            var Q2;
            Q2=qCreatedBy(makeId("Origin.pointOp"),VERTEX);
            transform(context, id + "F18", {"entities" : qUnion([Q0, Q1]), "transformType" : TransformType.SCALE_UNIFORMLY, "scale" : 2.5, "scalePoint" : qUnion([Q2]), "makeCopy" : false});
        }
    });
